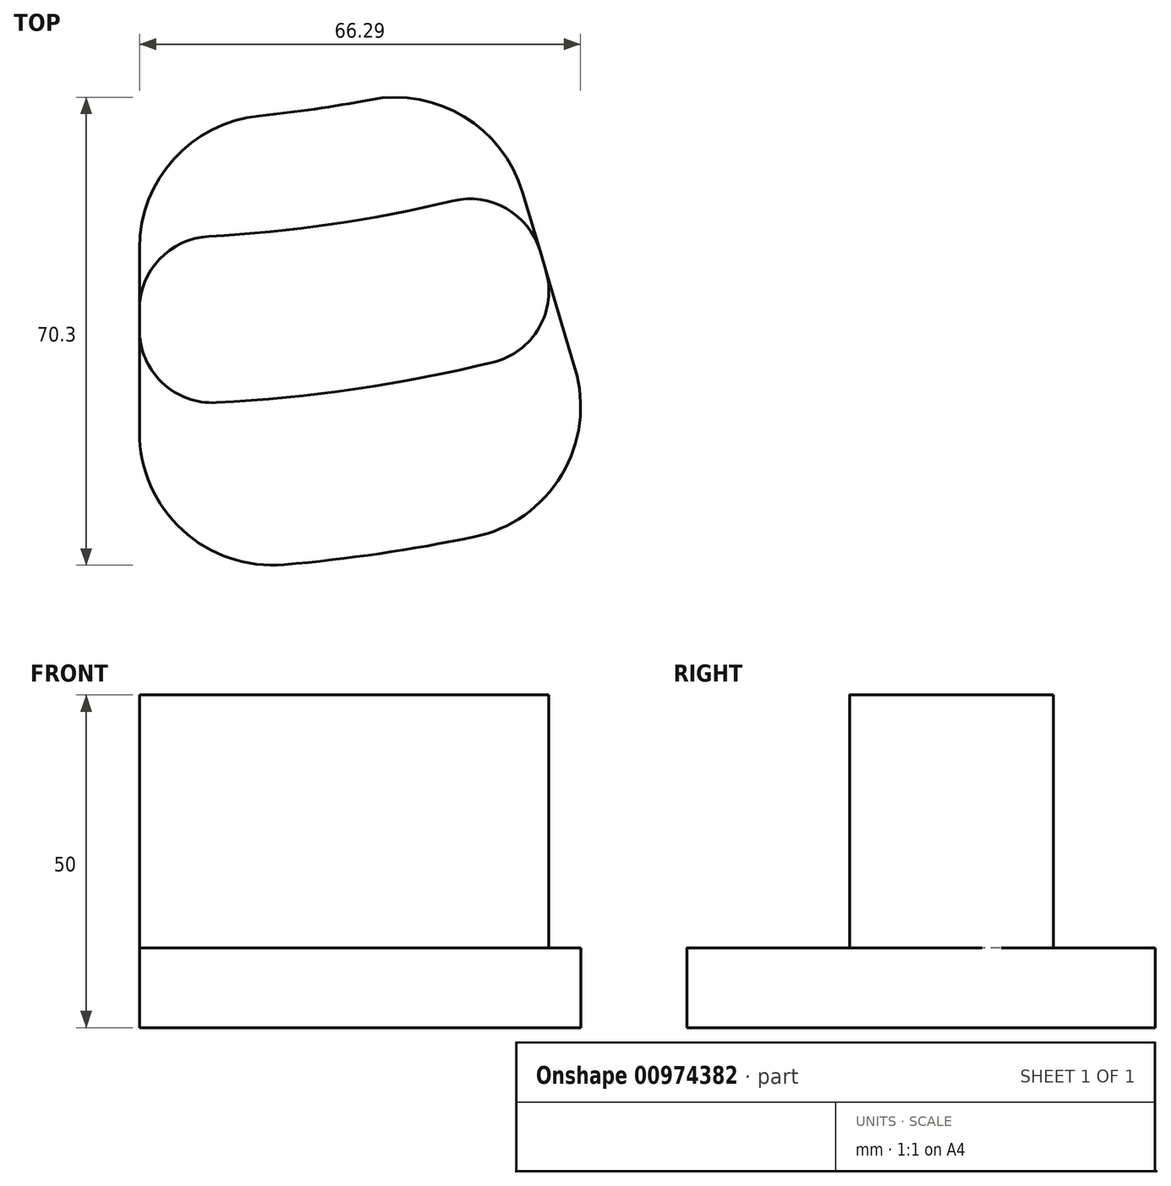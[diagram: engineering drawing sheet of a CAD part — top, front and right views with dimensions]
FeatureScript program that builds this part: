
annotation { "Feature Type Name" : "Feature", "Feature Type Description" : "" }
export const myFeature = defineFeature(function(context is Context, id is Id, definition is map)
    precondition{}
    {
        {
            var Q0;
            Q0=qCreatedBy(makeId("Top.planeOp"),FACE);
            var sketch = newSketch(context, id + "F0", { "sketchPlane" : qUnion([Q0])});
            skCircle(sketch, "E0", {"center": v(0, 0) * mm, "radius": 182.5 * mm});
            skCircle(sketch, "E1", {"center": v(0, 0) * mm, "radius": 250 * mm});
            skLineSegment(sketch, "E2", {"start": v(0, -182.5) * mm, "end": v(0, -250) * mm});
            skLineSegment(sketch, "E3", {"start": v(0, 0) * mm, "end": v(71.42, -239.58) * mm});
            skCircle(sketch, "E4", {"center": v(0, 0) * mm, "radius": 225 * mm});
            skCircle(sketch, "E5", {"center": v(0, 0) * mm, "radius": 200 * mm});
            skSolve(sketch);
        }
        {
            var Q0;
            {var subQ0=sQuery(id+"F0.wireOp",EDGE,"E2");var subQ1=sQuery(id+"F0.wireOp",EDGE,"E1");var subQ2=makeQuery(id+"F0.imprint","INTERSECT",VERTEX,{"derivedFrom":[subQ1,subQ0]});Q0=makeQuery(id+"F0.imprint","IMPRINT",FACE,{"disambiguationData":[TD([[makeQuery(id+"F0.imprint","IMPRINT",EDGE,{"disambiguationData":[TD([[subQ2,-1.0]])],"derivedFrom":subQ1}),1.0]])]});}
            var Q1;
            {var subQ0=sQuery(id+"F0.wireOp",EDGE,"E5");var subQ1=sQuery(id+"F0.wireOp",EDGE,"E2");var subQ2=makeQuery(id+"F0.imprint","INTERSECT",VERTEX,{"derivedFrom":[subQ1,subQ0]});Q1=makeQuery(id+"F0.imprint","IMPRINT",FACE,{"disambiguationData":[TD([[makeQuery(id+"F0.imprint","IMPRINT",EDGE,{"disambiguationData":[TD([[subQ2,-1.0]])],"derivedFrom":subQ1}),1.0]])]});}
            var Q2;
            {var subQ0=sQuery(id+"F0.wireOp",EDGE,"E2");var subQ1=sQuery(id+"F0.wireOp",EDGE,"E0");var subQ2=makeQuery(id+"F0.imprint","INTERSECT",VERTEX,{"derivedFrom":[subQ1,subQ0]});Q2=makeQuery(id+"F0.imprint","IMPRINT",FACE,{"disambiguationData":[TD([[makeQuery(id+"F0.imprint","IMPRINT",EDGE,{"disambiguationData":[TD([[subQ2,-1.0]])],"derivedFrom":subQ1}),-1.0]])]});}
            extrude(context, id + "F1", {"entities" : qUnion([Q0, Q1, Q2]), "depth" : 12 * mm, "offsetDistance" : 25 * mm});
        }
        {
            var Q0;
            {var subQ0=sQuery(id+"F0.wireOp",EDGE,"E5");var subQ1=sQuery(id+"F0.wireOp",EDGE,"E2");var subQ2=makeQuery(id+"F0.imprint","INTERSECT",VERTEX,{"derivedFrom":[subQ1,subQ0]});Q0=makeQuery(id+"F0.imprint","IMPRINT",FACE,{"disambiguationData":[TD([[makeQuery(id+"F0.imprint","IMPRINT",EDGE,{"disambiguationData":[TD([[subQ2,-1.0]])],"derivedFrom":subQ1}),1.0]])]});}
            extrude(context, id + "F2", {"entities" : qUnion([Q0]), "operationType" : NewBodyOperationType.ADD, "depth" : 50 * mm, "offsetDistance" : 25 * mm});
        }
        {
            var Q0;
            Q0=makeQuery(id+"F1.opExtrude","SWEPT_EDGE",EDGE,{"disambiguationData":[OSD([sQuery(id+"F0.wireOp",EDGE,"E1"),sQuery(id+"F0.wireOp",EDGE,"E2")])]});
            var Q1;
            Q1=makeQuery(id+"F1.opExtrude","SWEPT_EDGE",EDGE,{"disambiguationData":[OSD([sQuery(id+"F0.wireOp",EDGE,"E0"),sQuery(id+"F0.wireOp",EDGE,"E2")])]});
            var Q2;
            Q2=makeQuery(id+"F1.opExtrude","SWEPT_EDGE",EDGE,{"disambiguationData":[OSD([sQuery(id+"F0.wireOp",EDGE,"E0"),sQuery(id+"F0.wireOp",EDGE,"E3")])]});
            var Q3;
            Q3=makeQuery(id+"F1.opExtrude","SWEPT_EDGE",EDGE,{"disambiguationData":[OSD([sQuery(id+"F0.wireOp",EDGE,"E1"),sQuery(id+"F0.wireOp",EDGE,"E3")])]});
            fillet(context, id + "F3", {"entities" : qUnion([Q0, Q1, Q2, Q3]), "radius" : 20 * mm, "tangentPropagation" : true, "allowEdgeOverflow" : false});
        }
        {
            var Q0;
            Q0=makeQuery(id+"F3.opFillet","BLEND_EDGE",EDGE,{"blendedFrom":[makeQuery(id+"F1.opExtrude","SWEPT_EDGE",EDGE,{"disambiguationData":[OSD([sQuery(id+"F0.wireOp",EDGE,"E0"),sQuery(id+"F0.wireOp",EDGE,"E2")])]}),makeQuery(id+"F2.opExtrude","SWEPT_FACE",FACE,{"disambiguationData":[OSD([sQuery(id+"F0.wireOp",EDGE,"E5")])]})],"blendedInto":[makeQuery(id+"F2.opExtrude","SWEPT_FACE",FACE,{"disambiguationData":[OSD([sQuery(id+"F0.wireOp",EDGE,"E5")])]})]});
            var Q1;
            Q1=makeQuery(id+"F2.opExtrude","SWEPT_EDGE",EDGE,{"disambiguationData":[OSD([sQuery(id+"F0.wireOp",EDGE,"E2"),sQuery(id+"F0.wireOp",EDGE,"E4")])]});
            var Q2;
            Q2=makeQuery(id+"F3.opFillet","BLEND_EDGE",EDGE,{"blendedFrom":[makeQuery(id+"F1.opExtrude","SWEPT_EDGE",EDGE,{"disambiguationData":[OSD([sQuery(id+"F0.wireOp",EDGE,"E0"),sQuery(id+"F0.wireOp",EDGE,"E3")])]}),makeQuery(id+"F2.opExtrude","SWEPT_FACE",FACE,{"disambiguationData":[OSD([sQuery(id+"F0.wireOp",EDGE,"E5")])]})],"blendedInto":[makeQuery(id+"F2.opExtrude","SWEPT_FACE",FACE,{"disambiguationData":[OSD([sQuery(id+"F0.wireOp",EDGE,"E5")])]})]});
            var Q3;
            Q3=makeQuery(id+"F2.opExtrude","SWEPT_EDGE",EDGE,{"disambiguationData":[OSD([sQuery(id+"F0.wireOp",EDGE,"E3"),sQuery(id+"F0.wireOp",EDGE,"E4")])]});
            fillet(context, id + "F4", {"entities" : qUnion([Q0, Q1, Q2, Q3]), "radius" : 11 * mm, "tangentPropagation" : true, "allowEdgeOverflow" : false});
        }
    });
